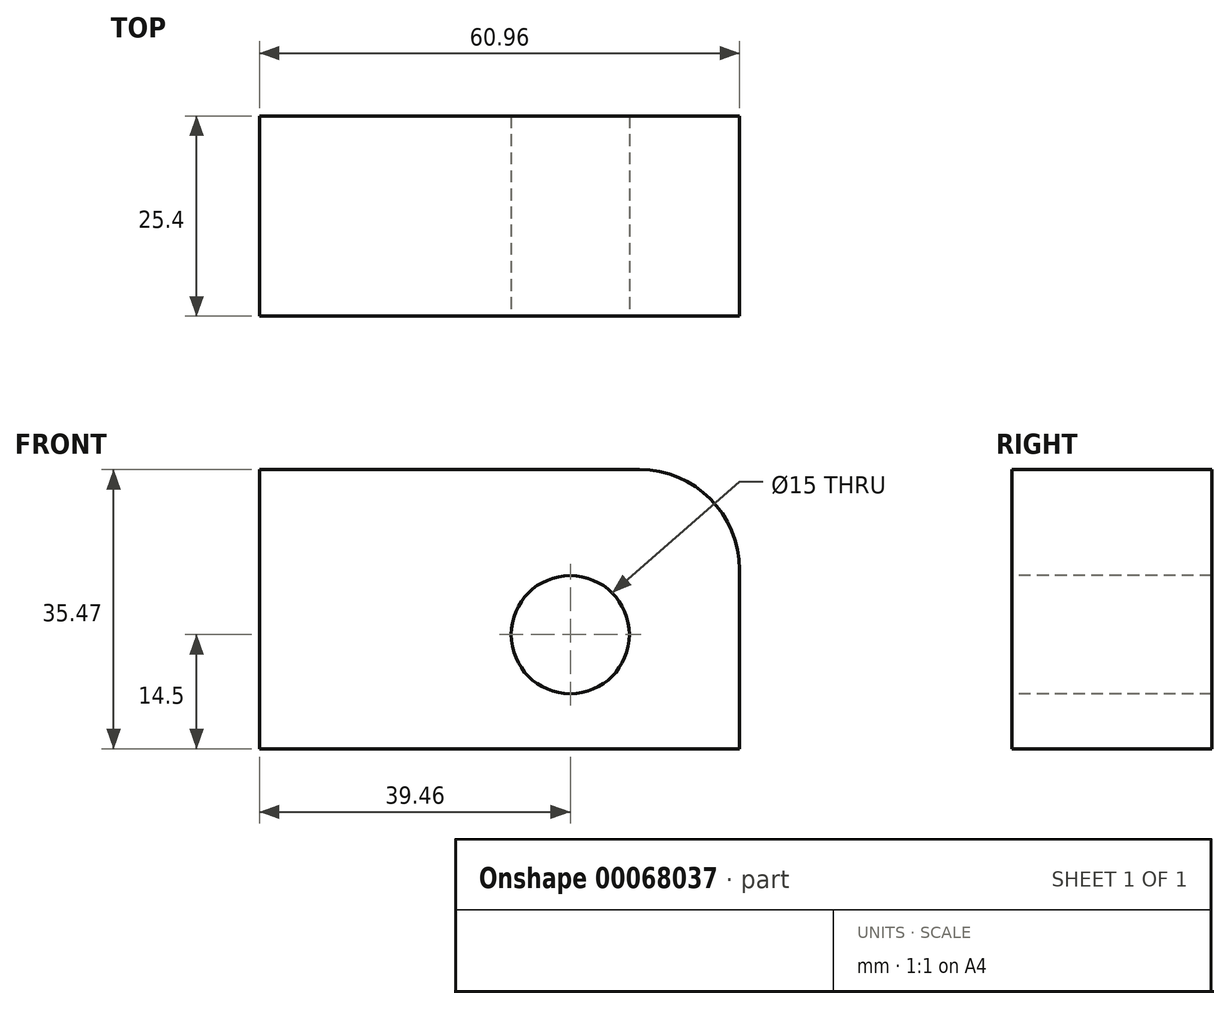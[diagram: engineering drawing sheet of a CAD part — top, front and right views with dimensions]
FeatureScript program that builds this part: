
annotation { "Feature Type Name" : "Feature", "Feature Type Description" : "" }
export const myFeature = defineFeature(function(context is Context, id is Id, definition is map)
    precondition{}
    {
        {
            var Q0;
            Q0=qCreatedBy(makeId("Front.planeOp"),FACE);
            var sketch = newSketch(context, id + "F0", { "sketchPlane" : qUnion([Q0])});
            skLineSegment(sketch, "E0.bottom", {"start": v(0, 0) * mm, "end": v(60.96, 0) * mm});
            skLineSegment(sketch, "E0.top", {"start": v(0, 35.47) * mm, "end": v(48.26, 35.47) * mm});
            skLineSegment(sketch, "E0.left", {"start": v(0, 0) * mm, "end": v(0, 35.47) * mm});
            skLineSegment(sketch, "E0.right", {"start": v(60.96, 0) * mm, "end": v(60.96, 22.77) * mm});
            skPoint(sketch, "E1.visualSharp", {"position": v(60.96, 35.47) * mm});
            skArc(sketch, "E1.filletArc", {"start": v(60.96, 22.77) * mm, "mid": v(57.24, 31.75) * mm, "end": v(48.26, 35.47) * mm});
            skSolve(sketch);
        }
        {
            var Q0;
            Q0 = qSketchRegion(id + "F0", true);
            extrude(context, id + "F1", {"entities" : qUnion([Q0]), "depth" : 25.4 * mm});
        }
        {
            var Q0;
            Q0=makeQuery(id+"F1.opExtrude","CAP_FACE",FACE,{"disambiguationData":[OSD([sQuery(id+"F0.wireOp",EDGE,"E0.bottom"),sQuery(id+"F0.wireOp",EDGE,"E0.top"),sQuery(id+"F0.wireOp",EDGE,"E0.left"),sQuery(id+"F0.wireOp",EDGE,"E0.right"),sQuery(id+"F0.wireOp",EDGE,"E1.filletArc")])],"isStart":false});
            var sketch = newSketch(context, id + "F2", { "sketchPlane" : qUnion([Q0])});
            skCircle(sketch, "E2", {"center": v(39.46, 14.5) * mm, "radius": 7.5 * mm});
            skSolve(sketch);
        }
        {
            var Q0;
            Q0 = qSketchRegion(id + "F2", true);
            extrude(context, id + "F3", {"entities" : qUnion([Q0]), "operationType" : NewBodyOperationType.REMOVE, "endBound" : BoundingType.THROUGH_ALL, "oppositeDirection" : true, "depth" : 25 * mm});
        }
    });
